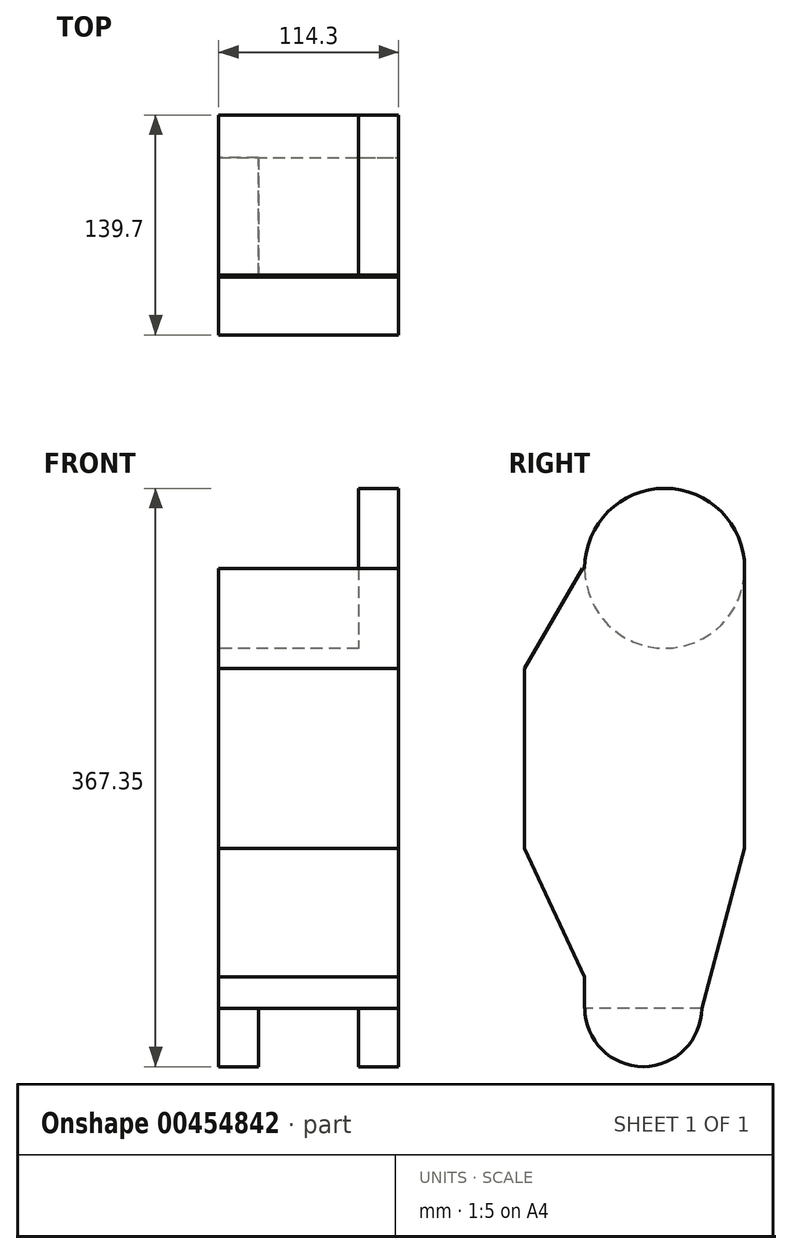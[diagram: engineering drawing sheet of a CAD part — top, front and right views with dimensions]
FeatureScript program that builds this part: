
annotation { "Feature Type Name" : "Feature", "Feature Type Description" : "" }
export const myFeature = defineFeature(function(context is Context, id is Id, definition is map)
    precondition{}
    {
        {
            var Q0;
            Q0=qCreatedBy(makeId("Right.planeOp"),FACE);
            var sketch = newSketch(context, id + "F0", { "sketchPlane" : qUnion([Q0])});
            skCircle(sketch, "E0", {"center": v(0, 0) * mm, "radius": 50.8 * mm});
            skLineSegment(sketch, "E1.bottom", {"start": v(50.8, 0) * mm, "end": v(-50.8, 0) * mm});
            skLineSegment(sketch, "E1.top", {"start": v(50.8, -101.6) * mm, "end": v(-50.8, -101.6) * mm});
            skLineSegment(sketch, "E1.left", {"start": v(50.8, 0) * mm, "end": v(50.8, -101.6) * mm});
            skLineSegment(sketch, "E1.right", {"start": v(-50.8, 0) * mm, "end": v(-50.8, -101.6) * mm});
            skPoint(sketch, "E1.middle", {"position": v(0, -50.8) * mm});
            skSolve(sketch);
        }
        {
            var Q0;
            Q0=makeQuery(id+"F0.imprint","IMPRINT",FACE,{"disambiguationData":[TD([[makeQuery(id+"F0.imprint","IMPRINT",EDGE,{"derivedFrom":sQuery(id+"F0.wireOp",EDGE,"E1.top")}),-1.0]])]});
            extrude(context, id + "F1", {"entities" : qUnion([Q0]), "depth" : 19.05 * mm, "offsetDistance" : 25.4 * mm});
        }
        {
            var Q0;
            Q0=makeQuery(id+"F0.imprint","IMPRINT",FACE,{"disambiguationData":[TD([[makeQuery(id+"F0.imprint","IMPRINT",EDGE,{"derivedFrom":sQuery(id+"F0.wireOp",EDGE,"E1.top")}),-1.0]])]});
            extrude(context, id + "F2", {"entities" : qUnion([Q0]), "operationType" : NewBodyOperationType.ADD, "depth" : 114.3 * mm, "offsetDistance" : 25.4 * mm});
        }
        {
            var Q0;
            {var subQ0=sQuery(id+"F0.wireOp",EDGE,"E1.top");Q0=makeQuery(id+"F2.boolean.opBoolean","MERGE",FACE,{"derivedFrom":[makeQuery(id+"F1.opExtrude","SWEPT_FACE",FACE,{"disambiguationData":[OSD([subQ0])]}),makeQuery(id+"F2.opExtrude","SWEPT_FACE",FACE,{"disambiguationData":[OSD([subQ0])]})]});}
            var sketch = newSketch(context, id + "F3", { "sketchPlane" : qUnion([Q0])});
            skLineSegment(sketch, "E2.bottom", {"start": v(0, 50.8) * mm, "end": v(114.3, 50.8) * mm});
            skLineSegment(sketch, "E2.top", {"start": v(0, -50.8) * mm, "end": v(114.3, -50.8) * mm});
            skLineSegment(sketch, "E2.left", {"start": v(0, 50.8) * mm, "end": v(0, -50.8) * mm});
            skLineSegment(sketch, "E2.right", {"start": v(114.3, 50.8) * mm, "end": v(114.3, -50.8) * mm});
            skSolve(sketch);
        }
        {
            var Q0;
            Q0=qSketchRegion(id+"F3",true);
            extrude(context, id + "F4", {"entities" : qUnion([Q0]), "operationType" : NewBodyOperationType.ADD, "depth" : 177.8 * mm, "offsetDistance" : 25.4 * mm});
        }
        {
            var Q0;
            Q0=makeQuery(id+"F4.opExtrude","CAP_EDGE",EDGE,{"disambiguationData":[OSD([sQuery(id+"F3.wireOp",EDGE,"E2.top")])],"isStart":false});
            chamfer(context, id + "F5", {"entities" : qUnion([Q0]), "chamferType" : ChamferType.OFFSET_ANGLE, "width" : 101.6 * mm, "oppositeDirection" : false, "angle" : 15 * degree, "tangentPropagation" : true});
        }
        {
            var Q0;
            Q0=makeQuery(id+"F4.boolean.opBoolean","MERGE",FACE,{"derivedFrom":[makeQuery(id+"F1.opExtrude","CAP_FACE",FACE,{"disambiguationData":[OSD([sQuery(id+"F0.wireOp",EDGE,"E0"),sQuery(id+"F0.wireOp",EDGE,"E1.top"),sQuery(id+"F0.wireOp",EDGE,"E1.left"),sQuery(id+"F0.wireOp",EDGE,"E1.right")])],"isStart":true}),makeQuery(id+"F4.opExtrude","SWEPT_FACE",FACE,{"disambiguationData":[OSD([sQuery(id+"F3.wireOp",EDGE,"E2.left")])]})]});
            var sketch = newSketch(context, id + "F6", { "sketchPlane" : qUnion([Q0])});
            skCircle(sketch, "E3", {"center": v(13.61, -279.4) * mm, "radius": 37.15 * mm});
            skSolve(sketch);
        }
        {
            var Q0;
            Q0=qSketchRegion(id+"F6",true);
            extrude(context, id + "F7", {"entities" : qUnion([Q0]), "operationType" : NewBodyOperationType.ADD, "oppositeDirection" : true, "depth" : 25.4 * mm, "offsetDistance" : 25.4 * mm});
        }
        {
            var Q0;
            Q0=makeQuery(id+"F4.boolean.opBoolean","MERGE",FACE,{"derivedFrom":[makeQuery(id+"F2.opExtrude","CAP_FACE",FACE,{"disambiguationData":[OSD([sQuery(id+"F0.wireOp",EDGE,"E0"),sQuery(id+"F0.wireOp",EDGE,"E1.top"),sQuery(id+"F0.wireOp",EDGE,"E1.left"),sQuery(id+"F0.wireOp",EDGE,"E1.right")])],"isStart":false}),makeQuery(id+"F4.opExtrude","SWEPT_FACE",FACE,{"disambiguationData":[OSD([sQuery(id+"F3.wireOp",EDGE,"E2.right")])]})]});
            var sketch = newSketch(context, id + "F8", { "sketchPlane" : qUnion([Q0])});
            skCircle(sketch, "E4", {"center": v(-13.61, -279.4) * mm, "radius": 37.15 * mm});
            skSolve(sketch);
        }
        {
            var Q0;
            Q0=qSketchRegion(id+"F8",true);
            extrude(context, id + "F9", {"entities" : qUnion([Q0]), "operationType" : NewBodyOperationType.ADD, "oppositeDirection" : true, "depth" : 25.4 * mm, "offsetDistance" : 25.4 * mm});
        }
        {
            var Q0;
            {var subQ0=sQuery(id+"F0.wireOp",EDGE,"E1.right");Q0=makeQuery(id+"F4.boolean.opBoolean","MERGE",FACE,{"derivedFrom":[makeQuery(id+"F2.boolean.opBoolean","MERGE",FACE,{"derivedFrom":[makeQuery(id+"F1.opExtrude","SWEPT_FACE",FACE,{"disambiguationData":[OSD([subQ0])]}),makeQuery(id+"F2.opExtrude","SWEPT_FACE",FACE,{"disambiguationData":[OSD([subQ0])]})]}),makeQuery(id+"F4.opExtrude","SWEPT_FACE",FACE,{"disambiguationData":[OSD([sQuery(id+"F3.wireOp",EDGE,"E2.bottom")])]})]});}
            var sketch = newSketch(context, id + "F10", { "sketchPlane" : qUnion([Q0])});
            skLineSegment(sketch, "E5.bottom", {"start": v(0, 0) * mm, "end": v(114.3, 0) * mm});
            skLineSegment(sketch, "E5.top", {"start": v(0, -266.7) * mm, "end": v(114.3, -266.7) * mm});
            skLineSegment(sketch, "E5.left", {"start": v(0, 0) * mm, "end": v(0, -266.7) * mm});
            skLineSegment(sketch, "E5.right", {"start": v(114.3, 0) * mm, "end": v(114.3, -266.7) * mm});
            skSolve(sketch);
        }
        {
            var Q0;
            Q0=qSketchRegion(id+"F10",true);
            extrude(context, id + "F11", {"entities" : qUnion([Q0]), "operationType" : NewBodyOperationType.ADD, "depth" : 38.1 * mm, "offsetDistance" : 25.4 * mm});
        }
        {
            var Q0;
            Q0=makeQuery(id+"F11.opExtrude","CAP_EDGE",EDGE,{"disambiguationData":[OSD([sQuery(id+"F10.wireOp",EDGE,"E5.top")])],"isStart":false});
            chamfer(context, id + "F12", {"entities" : qUnion([Q0]), "chamferType" : ChamferType.OFFSET_ANGLE, "width" : 88.9 * mm, "oppositeDirection" : false, "angle" : 25 * degree, "tangentPropagation" : true});
        }
        {
            var Q0;
            Q0=makeQuery(id+"F11.opExtrude","CAP_EDGE",EDGE,{"disambiguationData":[OSD([sQuery(id+"F10.wireOp",EDGE,"E5.bottom")])],"isStart":false});
            chamfer(context, id + "F13", {"entities" : qUnion([Q0]), "chamferType" : ChamferType.OFFSET_ANGLE, "width" : 63.5 * mm, "oppositeDirection" : false, "angle" : 30 * degree, "tangentPropagation" : true});
        }
        {
            var Q0;
            {var subQ0=sQuery(id+"F0.wireOp",EDGE,"E1.bottom");Q0=makeQuery(id+"F0.imprint","IMPRINT",FACE,{"disambiguationData":[TD([[makeQuery(id+"F0.imprint","IMPRINT",EDGE,{"derivedFrom":subQ0}),-1.0]])]});}
            var Q1;
            {var subQ0=sQuery(id+"F0.wireOp",EDGE,"E1.bottom");Q1=makeQuery(id+"F0.imprint","IMPRINT",FACE,{"disambiguationData":[TD([[makeQuery(id+"F0.imprint","IMPRINT",EDGE,{"derivedFrom":subQ0}),1.0]])]});}
            extrude(context, id + "F14", {"entities" : qUnion([Q0, Q1]), "operationType" : NewBodyOperationType.ADD, "depth" : 114.3 * mm, "offsetDistance" : 25.4 * mm, "hasSecondDirection" : true, "secondDirectionOppositeDirection" : false, "secondDirectionDepth" : 88.9 * mm});
        }
    });
